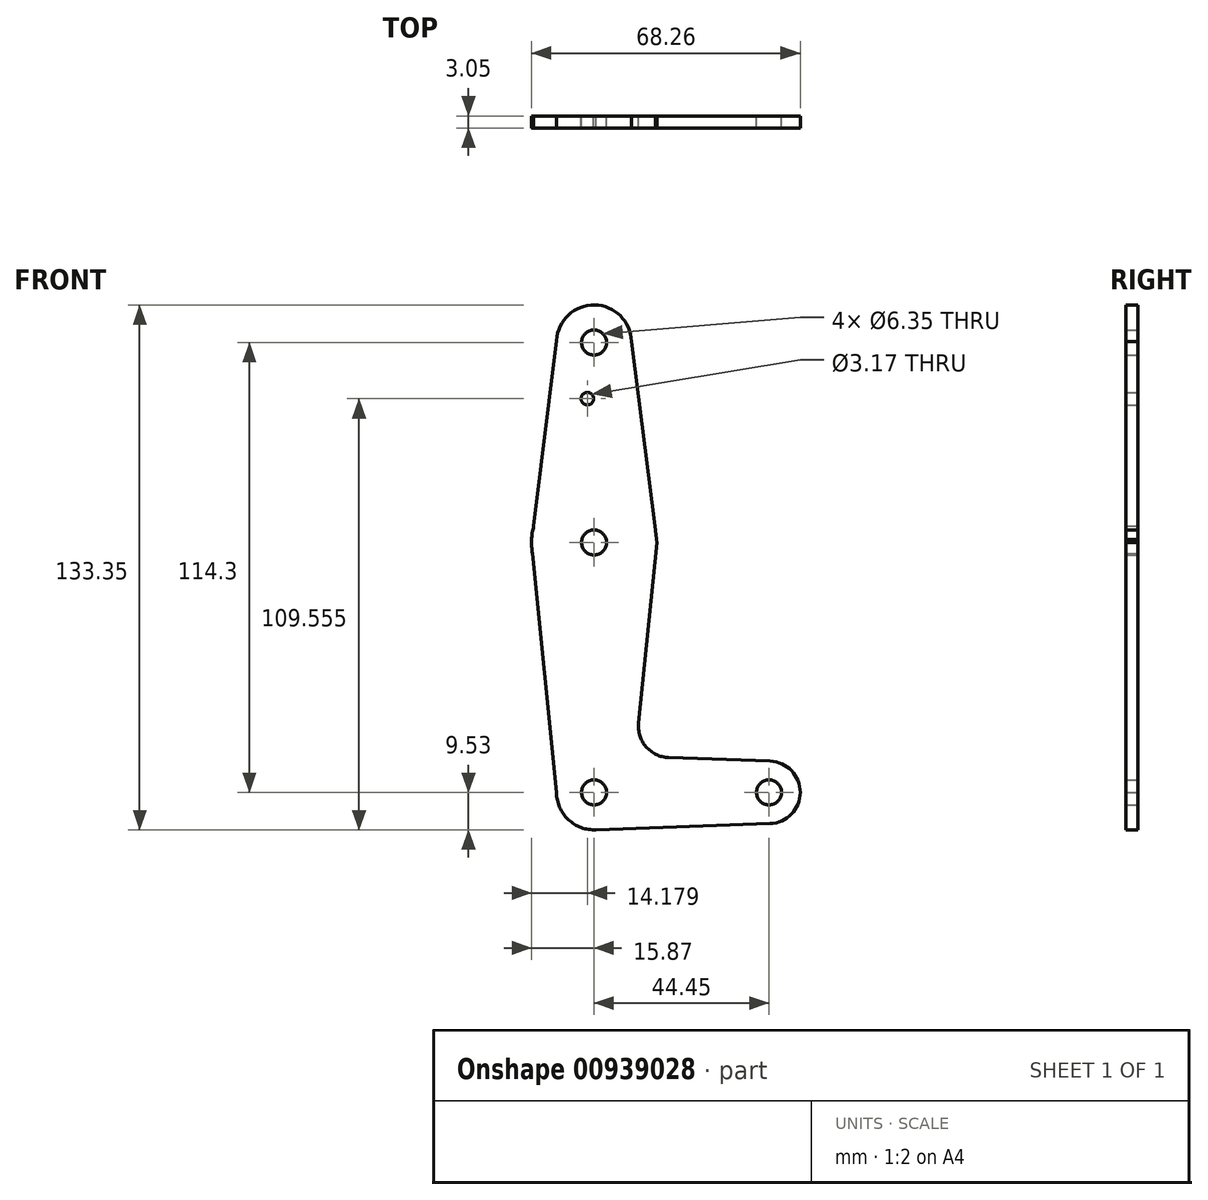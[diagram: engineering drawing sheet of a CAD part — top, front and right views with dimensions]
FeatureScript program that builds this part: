
annotation { "Feature Type Name" : "Feature", "Feature Type Description" : "" }
export const myFeature = defineFeature(function(context is Context, id is Id, definition is map)
    precondition{}
    {
        {
            var Q0;
            Q0=qCreatedBy(makeId("Front.planeOp"),FACE);
            var sketch = newSketch(context, id + "F0", { "sketchPlane" : qUnion([Q0])});
            skLineSegment(sketch, "E0", {"start": v(-37, 68.24) * mm, "end": v(-37, -46.06) * mm, "construction": true});
            skLineSegment(sketch, "E1", {"start": v(-37, -46.06) * mm, "end": v(7.45, -46.06) * mm, "construction": true});
            skCircle(sketch, "E2", {"center": v(-37, 68.24) * mm, "radius": 9.53 * mm});
            skCircle(sketch, "E3", {"center": v(-37, 17.44) * mm, "radius": 15.88 * mm});
            skCircle(sketch, "E4", {"center": v(-37, -46.06) * mm, "radius": 9.53 * mm});
            skCircle(sketch, "E5", {"center": v(7.45, -46.06) * mm, "radius": 7.94 * mm});
            skLineSegment(sketch, "E6", {"start": v(-46.52, -46.1) * mm, "end": v(-52.87, 17.13) * mm});
            skLineSegment(sketch, "E7", {"start": v(-25.7, -28.46) * mm, "end": v(-21.04, 17.44) * mm});
            skLineSegment(sketch, "E8", {"start": v(-27.71, 70.36) * mm, "end": v(-21.04, 17.44) * mm});
            skLineSegment(sketch, "E9", {"start": v(-46.51, 68.76) * mm, "end": v(-52.87, 17.13) * mm});
            skLineSegment(sketch, "E10", {"start": v(-18.07, -37.2) * mm, "end": v(7.73, -38.13) * mm});
            skLineSegment(sketch, "E11", {"start": v(-36.87, -55.58) * mm, "end": v(7.73, -54) * mm});
            skCircle(sketch, "E12", {"center": v(-37, 68.24) * mm, "radius": 3.18 * mm});
            skCircle(sketch, "E13", {"center": v(-37, 17.44) * mm, "radius": 3.18 * mm});
            skCircle(sketch, "E14", {"center": v(-37, -46.06) * mm, "radius": 3.18 * mm});
            skCircle(sketch, "E15", {"center": v(7.45, -46.06) * mm, "radius": 3.18 * mm});
            skCircle(sketch, "E16", {"center": v(-38.7, 53.96) * mm, "radius": 1.59 * mm});
            skArc(sketch, "E17.filletArc", {"start": v(-25.7, -28.46) * mm, "mid": v(-23.77, -34.49) * mm, "end": v(-18.07, -37.2) * mm});
            skSolve(sketch);
        }
        {
            var Q0;
            Q0 = qSketchRegion(id + "F0", true);
            extrude(context, id + "F1", {"entities" : qUnion([Q0]), "depth" : 3.05 * mm, "offsetDistance" : 25.4 * mm});
        }
    });
